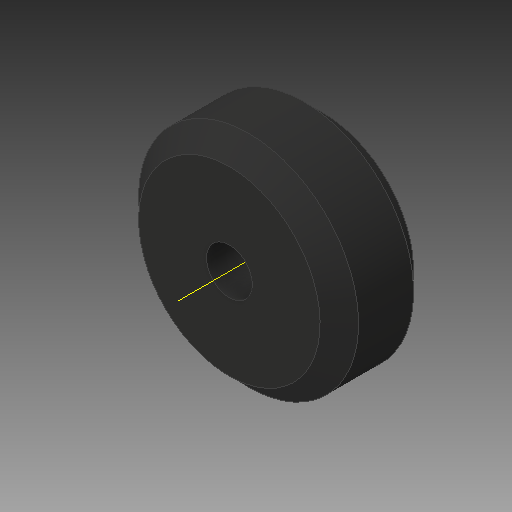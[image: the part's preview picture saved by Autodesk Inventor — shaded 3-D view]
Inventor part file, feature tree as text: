
AUTODESK INVENTOR PART (.ipt)
format: ipt  version: 2019 (Build 230136000, 136)  size: 113,152 bytes
history: native  units: in
note: dims shown in document units (in); Inventor stores cm internally (conversion verified against a paired STEP export)
features: revolve x1, other x1, sketch x1
ambient origin geometry x8: Origin, YZ Plane, XZ Plane, XY Plane, X Axis, Y Axis, Z Axis, Center Point
bodies: Solid1 (feature_tree)
feature tree (3):
  revolve  "Revolution1"  [1 undecoded]
  other  "Work Axis1"
  sketch  "Sketch2"  dims[d5=0.2362in d8=0.4016in d11=90.0deg]
note: 1 required parameter value undecoded (feature->parameter linkage not recoverable at this tier; creation-order binding heuristic only, values carry confidence <= 0.55)
